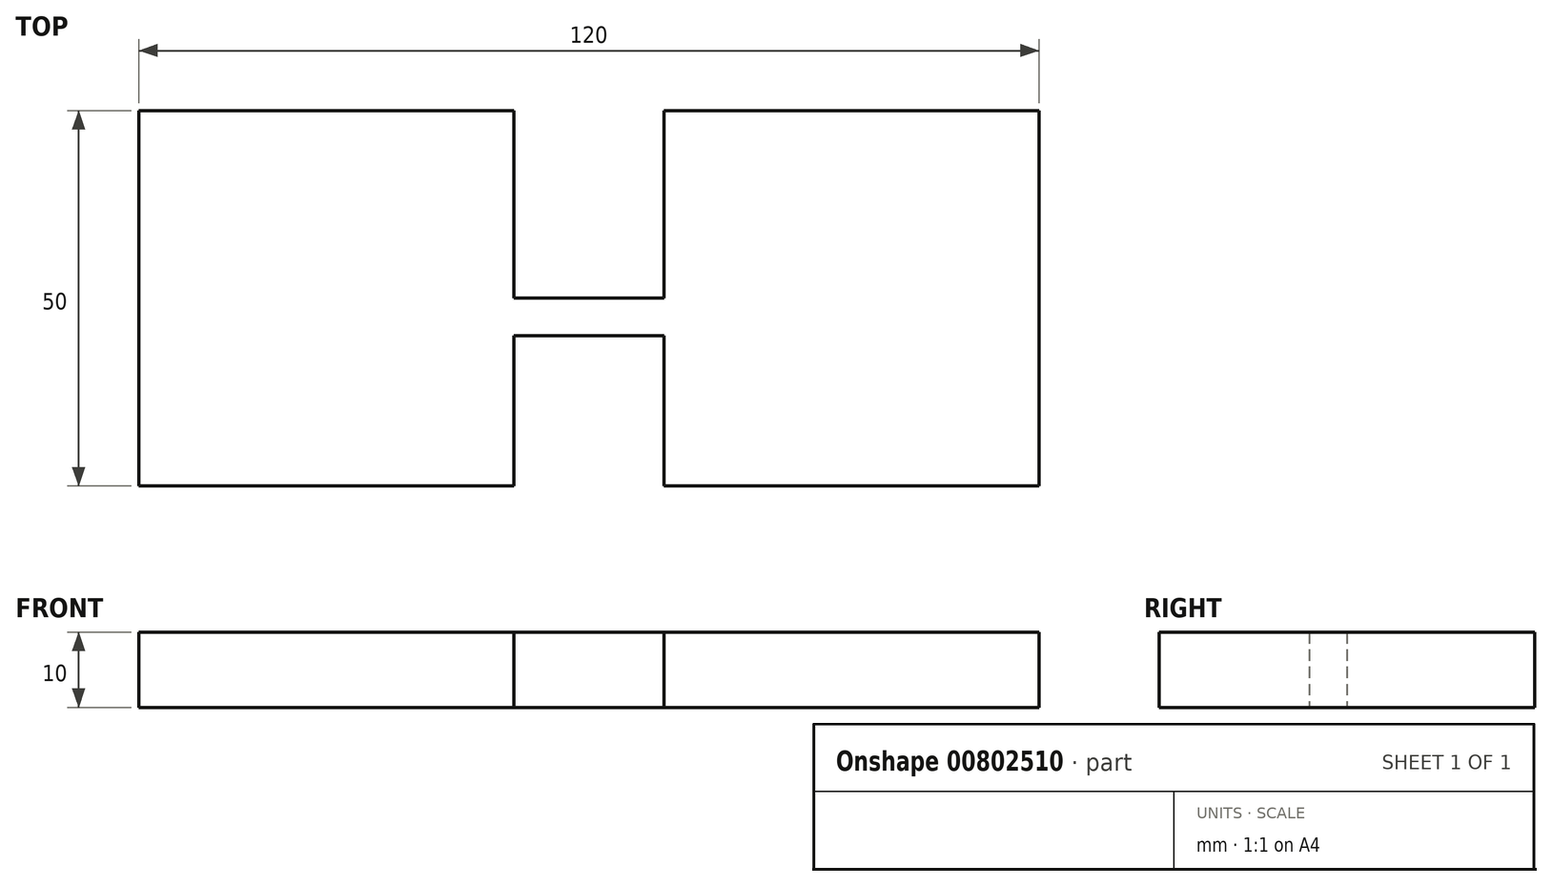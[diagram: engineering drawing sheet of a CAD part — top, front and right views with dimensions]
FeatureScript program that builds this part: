
annotation { "Feature Type Name" : "Feature", "Feature Type Description" : "" }
export const myFeature = defineFeature(function(context is Context, id is Id, definition is map)
    precondition{}
    {
        {
            var Q0;
            Q0=qCreatedBy(makeId("Top.planeOp"),FACE);
            var sketch = newSketch(context, id + "F0", { "sketchPlane" : qUnion([Q0])});
            skLineSegment(sketch, "E0.bottom", {"start": v(25, -25) * mm, "end": v(-25, -25) * mm});
            skLineSegment(sketch, "E0.top", {"start": v(25, 25) * mm, "end": v(-25, 25) * mm});
            skLineSegment(sketch, "E0.left", {"start": v(25, -25) * mm, "end": v(25, 25) * mm});
            skLineSegment(sketch, "E0.right", {"start": v(-25, -25) * mm, "end": v(-25, 25) * mm});
            skPoint(sketch, "E0.middle", {"position": v(0, 0) * mm});
            skLineSegment(sketch, "E1.bottom", {"start": v(45, -25) * mm, "end": v(95, -25) * mm});
            skLineSegment(sketch, "E1.top", {"start": v(45, 25) * mm, "end": v(95, 25) * mm});
            skLineSegment(sketch, "E1.left", {"start": v(45, -25) * mm, "end": v(45, 25) * mm});
            skLineSegment(sketch, "E1.right", {"start": v(95, -25) * mm, "end": v(95, 25) * mm});
            skLineSegment(sketch, "E2.bottom", {"start": v(25, -5) * mm, "end": v(45, -5) * mm});
            skLineSegment(sketch, "E2.top", {"start": v(25, 0) * mm, "end": v(45, 0) * mm});
            skLineSegment(sketch, "E2.left", {"start": v(25, -5) * mm, "end": v(25, 0) * mm});
            skLineSegment(sketch, "E2.right", {"start": v(45, -5) * mm, "end": v(45, 0) * mm});
            skSolve(sketch);
        }
        {
            var Q0;
            Q0=makeQuery(id+"F0.imprint","IMPRINT",FACE,{"disambiguationData":[TD([[makeQuery(id+"F0.imprint","IMPRINT",EDGE,{"derivedFrom":sQuery(id+"F0.wireOp",EDGE,"E0.bottom")}),-1.0]])]});
            var Q1;
            Q1=makeQuery(id+"F0.imprint","IMPRINT",FACE,{"disambiguationData":[TD([[makeQuery(id+"F0.imprint","IMPRINT",EDGE,{"derivedFrom":sQuery(id+"F0.wireOp",EDGE,"E1.bottom")}),1.0]])]});
            var Q2;
            Q2=makeQuery(id+"F0.imprint","IMPRINT",FACE,{"disambiguationData":[TD([[makeQuery(id+"F0.imprint","IMPRINT",EDGE,{"derivedFrom":sQuery(id+"F0.wireOp",EDGE,"E2.bottom")}),1.0]])]});
            extrude(context, id + "F1", {"entities" : qUnion([Q0, Q1, Q2]), "depth" : 10 * mm, "offsetDistance" : 25 * mm});
        }
    });
